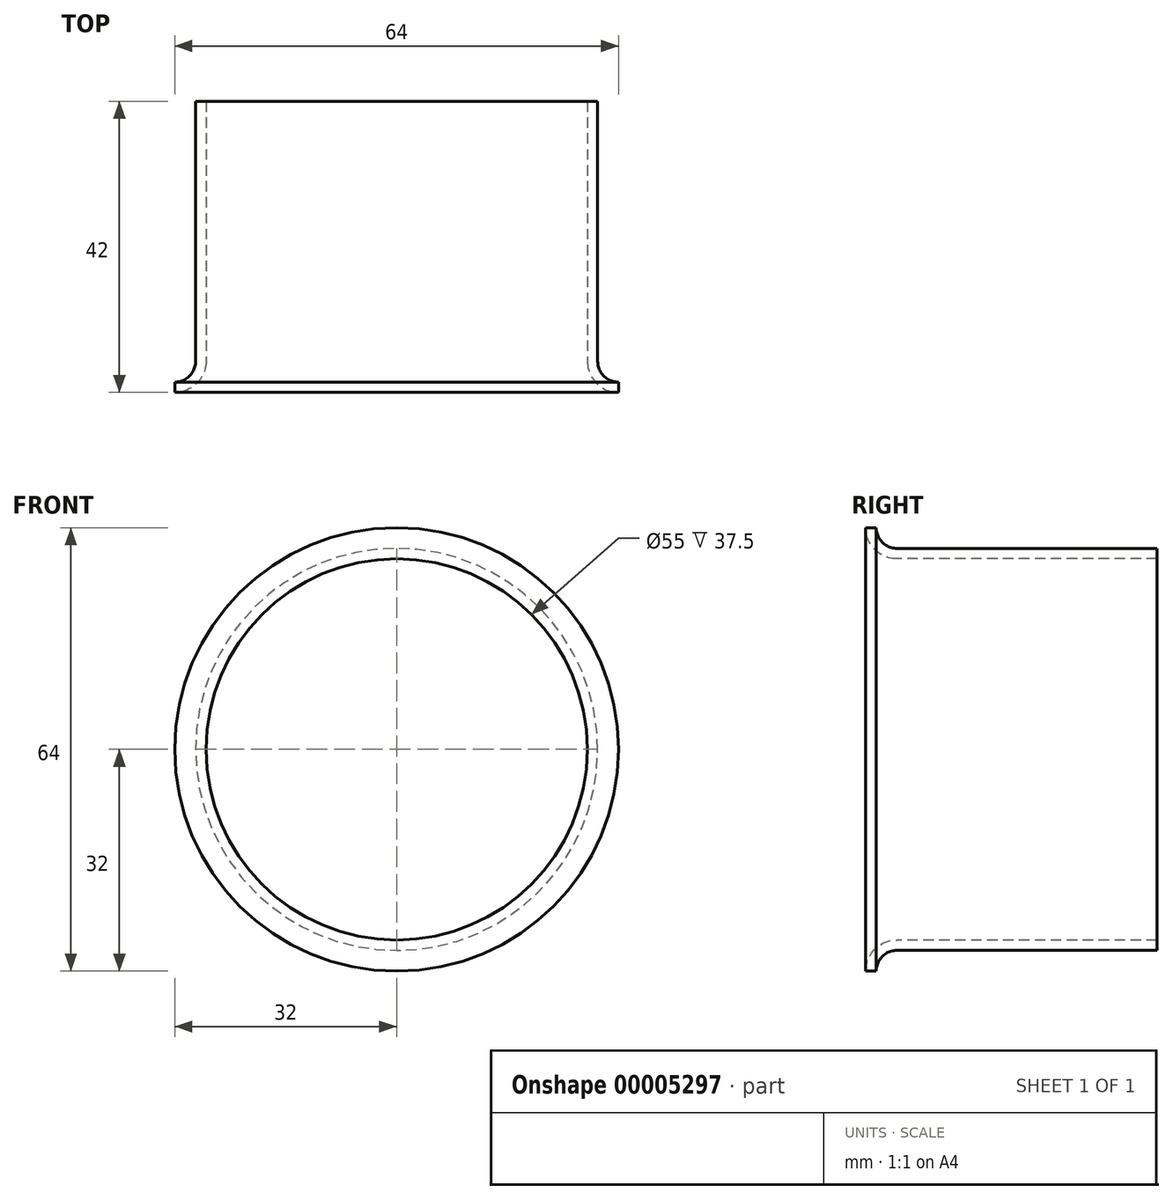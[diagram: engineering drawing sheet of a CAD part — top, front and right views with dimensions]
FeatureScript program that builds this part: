
annotation { "Feature Type Name" : "Feature", "Feature Type Description" : "" }
export const myFeature = defineFeature(function(context is Context, id is Id, definition is map)
    precondition{}
    {
        {
            var Q0;
            Q0=qCreatedBy(makeId("Right.planeOp"),FACE);
            var sketch = newSketch(context, id + "F0", { "sketchPlane" : qUnion([Q0])});
            skLineSegment(sketch, "E0", {"start": v(0, 27.5) * mm, "end": v(37.5, 27.5) * mm});
            skLineSegment(sketch, "E1", {"start": v(37.5, 27.5) * mm, "end": v(37.5, 29) * mm});
            skLineSegment(sketch, "E2", {"start": v(37.5, 29) * mm, "end": v(0, 29) * mm});
            skArc(sketch, "E3", {"start": v(0, 29) * mm, "mid": v(-2.12, 29.88) * mm, "end": v(-3, 32) * mm});
            skLineSegment(sketch, "E4", {"start": v(-3, 32) * mm, "end": v(-4.5, 32) * mm});
            skArc(sketch, "E5", {"start": v(0, 27.5) * mm, "mid": v(-3.18, 28.82) * mm, "end": v(-4.5, 32) * mm});
            skLineSegment(sketch, "E6", {"start": v(0, 0) * mm, "end": v(37.5, 0) * mm, "construction": true});
            skSolve(sketch);
        }
        {
            var Q0;
            Q0=makeQuery(id+"F0.imprint","IMPRINT",FACE,{"disambiguationData":[TD([[makeQuery(id+"F0.imprint","IMPRINT",EDGE,{"derivedFrom":sQuery(id+"F0.wireOp",EDGE,"E0")}),1.0]])]});
            var Q1;
            Q1=sQuery(id+"F0.wireOp",EDGE,"E6");
            revolve(context, id + "F1", {"entities" : qUnion([Q0]), "axis" : qUnion([Q1]), "revolveType" : RevolveType.FULL});
        }
    });
